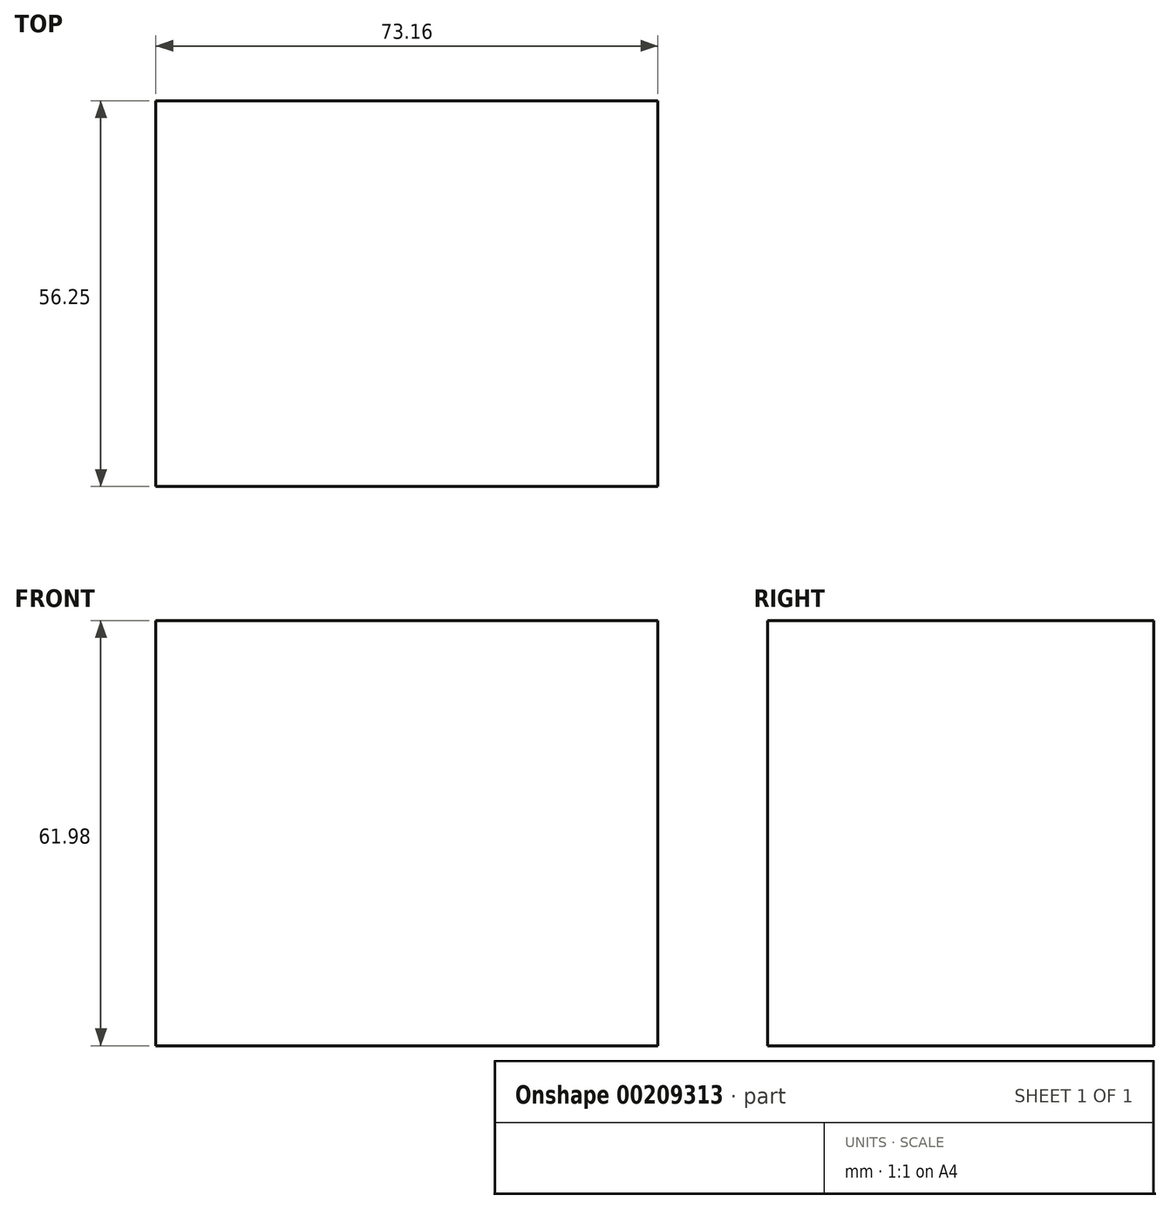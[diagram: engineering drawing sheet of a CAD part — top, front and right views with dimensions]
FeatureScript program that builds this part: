
annotation { "Feature Type Name" : "Feature", "Feature Type Description" : "" }
export const myFeature = defineFeature(function(context is Context, id is Id, definition is map)
    precondition{}
    {
        {
            var Q0;
            Q0=qCreatedBy(makeId("Top.planeOp"),FACE);
            var sketch = newSketch(context, id + "F0", { "sketchPlane" : qUnion([Q0])});
            skLineSegment(sketch, "E0.bottom", {"start": v(-35.56, 21.42) * mm, "end": v(37.6, 21.42) * mm});
            skLineSegment(sketch, "E0.top", {"start": v(-35.56, -34.83) * mm, "end": v(37.6, -34.83) * mm});
            skLineSegment(sketch, "E0.left", {"start": v(-35.56, 21.42) * mm, "end": v(-35.56, -34.83) * mm});
            skLineSegment(sketch, "E0.right", {"start": v(37.6, 21.42) * mm, "end": v(37.6, -34.83) * mm});
            skSolve(sketch);
        }
        {
            var Q0;
            Q0=makeQuery(id+"F0.imprint","IMPRINT",FACE,{"disambiguationData":[TD([[makeQuery(id+"F0.imprint","IMPRINT",EDGE,{"derivedFrom":sQuery(id+"F0.wireOp",EDGE,"E0.bottom")}),-1.0]])]});
            extrude(context, id + "F1", {"entities" : qUnion([Q0]), "depth" : 61.98 * mm});
        }
    });
